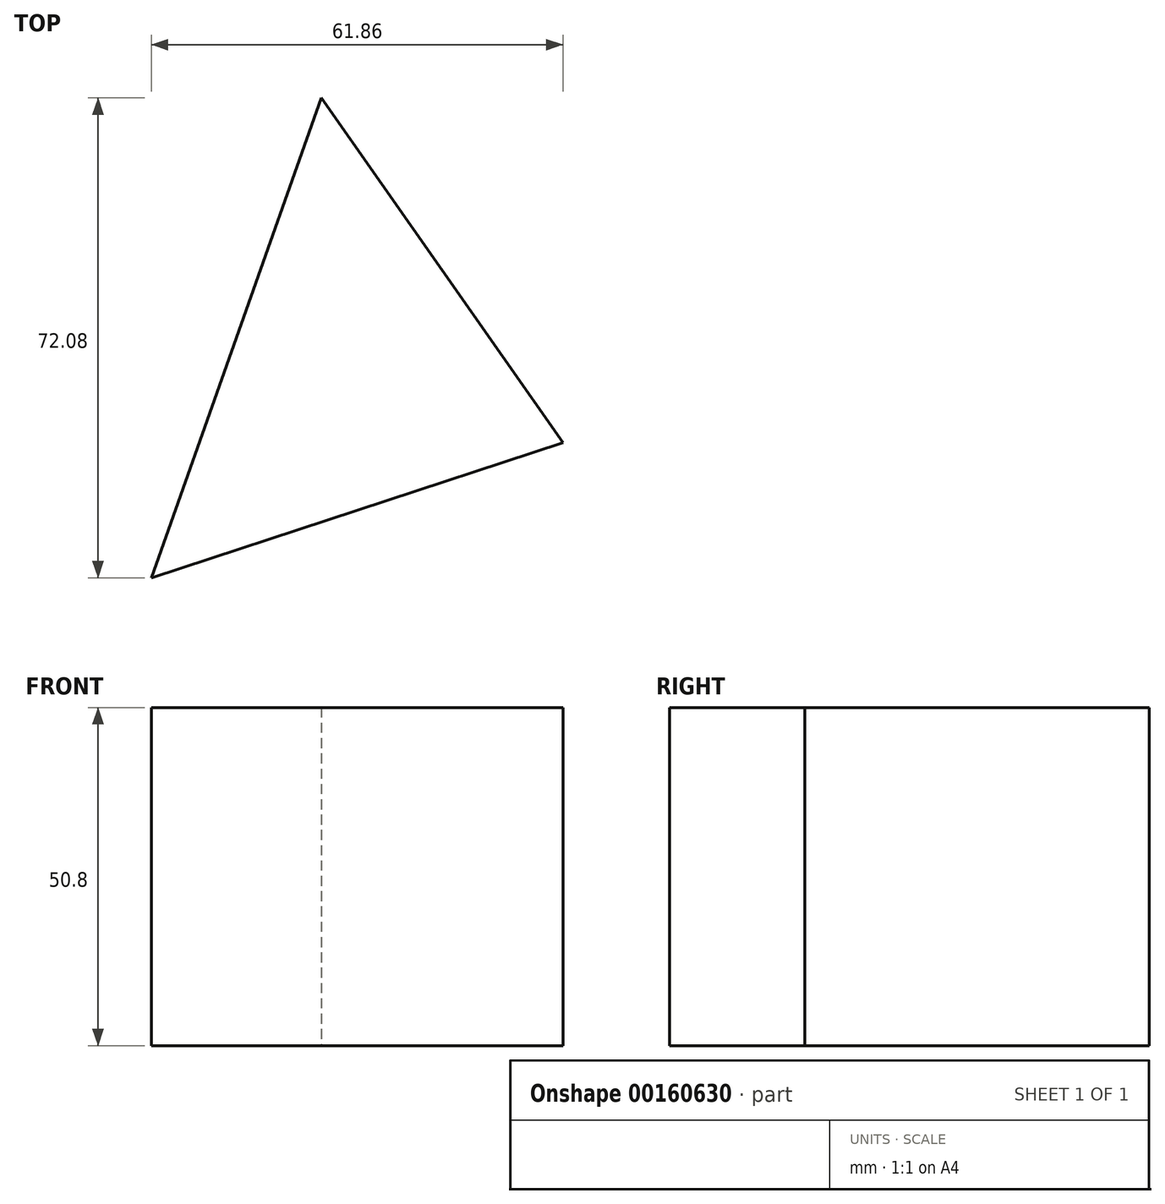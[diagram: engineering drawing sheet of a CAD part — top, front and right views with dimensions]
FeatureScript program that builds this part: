
annotation { "Feature Type Name" : "Feature", "Feature Type Description" : "" }
export const myFeature = defineFeature(function(context is Context, id is Id, definition is map)
    precondition{}
    {
        {
            var Q0;
            Q0=qCreatedBy(makeId("Top.planeOp"),FACE);
            var sketch = newSketch(context, id + "F0", { "sketchPlane" : qUnion([Q0])});
            skLineSegment(sketch, "E0", {"start": v(-31.6, -34.93) * mm, "end": v(-6.05, 37.15) * mm});
            skLineSegment(sketch, "E1", {"start": v(-6.05, 37.15) * mm, "end": v(30.26, -14.62) * mm});
            skLineSegment(sketch, "E2", {"start": v(30.26, -14.62) * mm, "end": v(-31.6, -34.93) * mm});
            skSolve(sketch);
        }
        {
            var Q0;
            Q0 = qSketchRegion(id + "F0", true);
            extrude(context, id + "F1", {"entities" : qUnion([Q0]), "depth" : 25.4 * mm});
        }
        {
            var Q0;
            Q0=makeQuery(id+"F1.opExtrude","CAP_FACE",FACE,{"disambiguationData":[OSD([sQuery(id+"F0.wireOp",EDGE,"E0"),sQuery(id+"F0.wireOp",EDGE,"E1"),sQuery(id+"F0.wireOp",EDGE,"E2")])],"isStart":false});
            var sketch = newSketch(context, id + "F2", { "sketchPlane" : qUnion([Q0])});
            skLineSegment(sketch, "E3.0", {"start": v(-31.6, -34.93) * mm, "end": v(-6.05, 37.15) * mm});
            skLineSegment(sketch, "E4.0", {"start": v(30.26, -14.62) * mm, "end": v(-31.6, -34.93) * mm});
            skLineSegment(sketch, "E5.0", {"start": v(-6.05, 37.15) * mm, "end": v(30.26, -14.62) * mm});
            skSolve(sketch);
        }
        {
            var Q0;
            Q0=makeQuery(id+"F2.imprint","IMPRINT",FACE,{"disambiguationData":[TD([[makeQuery(id+"F2.imprint","IMPRINT",EDGE,{"derivedFrom":sQuery(id+"F2.wireOp",EDGE,"E3.0")}),-1.0]])]});
            extrude(context, id + "F3", {"entities" : qUnion([Q0]), "operationType" : NewBodyOperationType.ADD, "depth" : 25.4 * mm});
        }
    });
